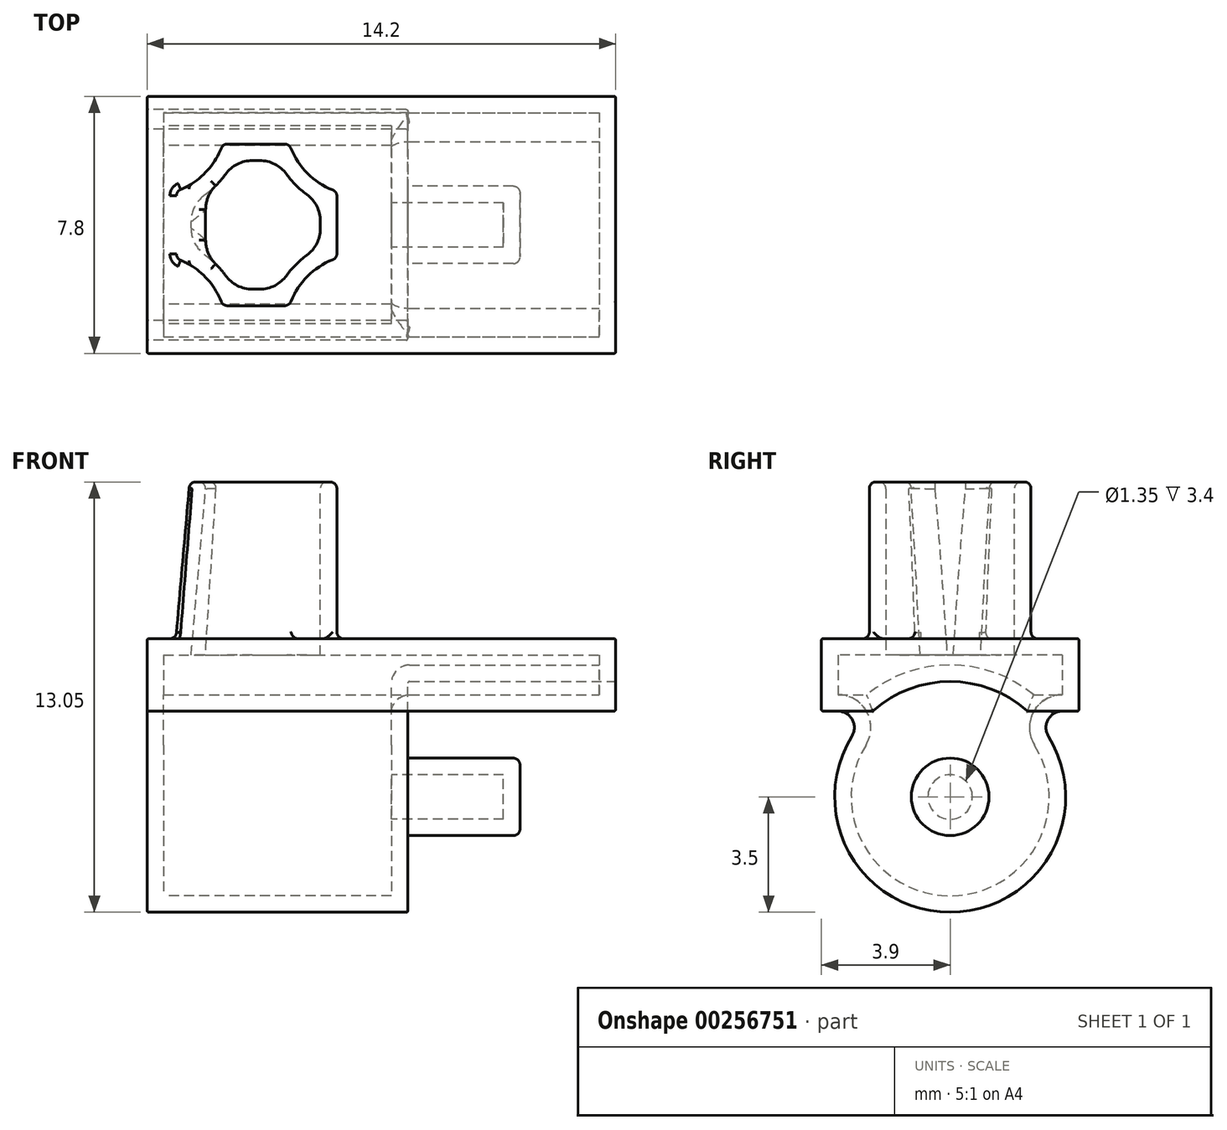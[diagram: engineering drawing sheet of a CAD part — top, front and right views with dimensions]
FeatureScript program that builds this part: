
annotation { "Feature Type Name" : "Feature", "Feature Type Description" : "" }
export const myFeature = defineFeature(function(context is Context, id is Id, definition is map)
    precondition{}
    {
        {
            var Q0;
            Q0=qCreatedBy(makeId("Right.planeOp"),FACE);
            var sketch = newSketch(context, id + "F0", { "sketchPlane" : qUnion([Q0])});
            skArc(sketch, "E0", {"start": v(-2.34, 2.6) * mm, "mid": v(0, -3.5) * mm, "end": v(2.34, 2.6) * mm});
            skLineSegment(sketch, "E1", {"start": v(-3.9, 4.8) * mm, "end": v(3.9, 4.8) * mm});
            skPoint(sketch, "E2", {"position": v(0, 4.8) * mm});
            skLineSegment(sketch, "E3", {"start": v(-3.9, 2.6) * mm, "end": v(-2.34, 2.6) * mm});
            skLineSegment(sketch, "E4", {"start": v(-3.9, 2.6) * mm, "end": v(-3.9, 4.8) * mm});
            skLineSegment(sketch, "E5", {"start": v(3.9, 2.6) * mm, "end": v(3.9, 4.8) * mm});
            skLineSegment(sketch, "E6.trimOffspring", {"start": v(2.34, 2.6) * mm, "end": v(3.9, 2.6) * mm});
            skSolve(sketch);
        }
        {
            var Q0;
            Q0=makeQuery(id+"F0.imprint","IMPRINT",FACE,{"disambiguationData":[TD([[makeQuery(id+"F0.imprint","IMPRINT",EDGE,{"derivedFrom":sQuery(id+"F0.wireOp",EDGE,"E0")}),1.0]])]});
            extrude(context, id + "F1", {"entities" : qUnion([Q0]), "depth" : 14.2 * mm, "symmetric" : true});
        }
        {
            var Q0;
            Q0=makeQuery(id+"F1.opExtrude","CAP_FACE",FACE,{"disambiguationData":[OSD([sQuery(id+"F0.wireOp",EDGE,"E0"),sQuery(id+"F0.wireOp",EDGE,"E1"),sQuery(id+"F0.wireOp",EDGE,"E3"),sQuery(id+"F0.wireOp",EDGE,"E4"),sQuery(id+"F0.wireOp",EDGE,"E5"),sQuery(id+"F0.wireOp",EDGE,"E6.trimOffspring")])],"isStart":false});
            var sketch = newSketch(context, id + "F2", { "sketchPlane" : qUnion([Q0])});
            skCircle(sketch, "E7", {"center": v(0, 0) * mm, "radius": 3.5 * mm});
            skSolve(sketch);
        }
        {
            var Q0;
            {var subQ0=sQuery(id+"F2.wireOp",EDGE,"E7");var subQ1=makeQuery(id+"F2.imprint","INTERSECT",VERTEX,{"derivedFrom":[makeQuery(id+"F1.opExtrude","CAP_EDGE",EDGE,{"disambiguationData":[OSD([sQuery(id+"F0.wireOp",EDGE,"E3")])],"isStart":false}),subQ0]});Q0=makeQuery(id+"F2.imprint","IMPRINT",FACE,{"disambiguationData":[TD([[makeQuery(id+"F2.imprint","IMPRINT",EDGE,{"disambiguationData":[TD([[subQ1,-1.0]])],"derivedFrom":subQ0}),1.0]])]});}
            extrude(context, id + "F3", {"entities" : qUnion([Q0]), "operationType" : NewBodyOperationType.REMOVE, "oppositeDirection" : true, "depth" : 6.3 * mm});
        }
        {
            var Q0;
            {var subQ0=sQuery(id+"F0.wireOp",EDGE,"E0");var subQ1=makeQuery(id+"F1.opExtrude","SWEPT_FACE",FACE,{"disambiguationData":[OSD([subQ0])]});var subQ2=sQuery(id+"F0.wireOp",EDGE,"E3");Q0=makeQuery(id+"FiiATRbnGKAqu3H_1.1.F3.boolean.opBoolean","SPLIT",EDGE,{"disambiguationData":[topologyDisambiguationEdgeConnected([subQ1])],"derivedFrom":makeQuery(id+"F3.boolean.opBoolean","SPLIT",EDGE,{"disambiguationData":[topologyDisambiguationEdgeConnected([subQ1])],"derivedFrom":makeQuery(id+"F1.opExtrude","SWEPT_EDGE",EDGE,{"disambiguationData":[OSD([subQ0,subQ2])]})})});}
            var Q1;
            {var subQ0=sQuery(id+"F0.wireOp",EDGE,"E0");var subQ1=makeQuery(id+"F1.opExtrude","SWEPT_FACE",FACE,{"disambiguationData":[OSD([subQ0])]});var subQ2=sQuery(id+"F0.wireOp",EDGE,"E6.trimOffspring");Q1=makeQuery(id+"FiiATRbnGKAqu3H_1.1.F3.boolean.opBoolean","SPLIT",EDGE,{"disambiguationData":[topologyDisambiguationEdgeConnected([subQ1])],"derivedFrom":makeQuery(id+"F3.boolean.opBoolean","SPLIT",EDGE,{"disambiguationData":[topologyDisambiguationEdgeConnected([subQ1])],"derivedFrom":makeQuery(id+"F1.opExtrude","SWEPT_EDGE",EDGE,{"disambiguationData":[OSD([subQ0,subQ2])]})})});}
            fillet(context, id + "F4", {"entities" : qUnion([Q0, Q1]), "radius" : 0.5 * mm, "tangentPropagation" : true, "allowEdgeOverflow" : false});
        }
        {
            var Q0;
            Q0=makeQuery(id+"F3.boolean.opBoolean","COPY",FACE,{"derivedFrom":makeQuery(id+"F3.opExtrude","CAP_FACE",FACE,{"disambiguationData":[OSD([sQuery(id+"F2.wireOp",EDGE,"E7")])],"isStart":false})});
            var Q1;
            Q1=makeQuery(id+"FiiATRbnGKAqu3H_1.1.F3.boolean.opBoolean","COPY",FACE,{"derivedFrom":makeQuery(id+"FiiATRbnGKAqu3H_1.1.F3.opExtrude","CAP_FACE",FACE,{"disambiguationData":[OSD([sQuery(id+"F2.wireOp",EDGE,"E7")])],"isStart":false})});
            var Q2;
            Q2=makeQuery(id+"F3.boolean.opBoolean","COPY",FACE,{"derivedFrom":makeQuery(id+"F3.opExtrude","SWEPT_FACE",FACE,{"disambiguationData":[OSD([sQuery(id+"F2.wireOp",EDGE,"E7")])]})});
            var Q3;
            Q3=makeQuery(id+"FiiATRbnGKAqu3H_1.1.F3.boolean.opBoolean","COPY",FACE,{"derivedFrom":makeQuery(id+"FiiATRbnGKAqu3H_1.1.F3.opExtrude","SWEPT_FACE",FACE,{"disambiguationData":[OSD([sQuery(id+"F2.wireOp",EDGE,"E7")])]})});
            var Q4;
            Q4=makeQuery(id+"F1.opExtrude","SWEPT_FACE",FACE,{"disambiguationData":[OSD([sQuery(id+"F0.wireOp",EDGE,"E3")])]});
            var Q5;
            Q5=makeQuery(id+"F1.opExtrude","SWEPT_FACE",FACE,{"disambiguationData":[OSD([sQuery(id+"F0.wireOp",EDGE,"E4")])]});
            var Q6;
            Q6=makeQuery(id+"F1.opExtrude","CAP_FACE",FACE,{"disambiguationData":[OSD([sQuery(id+"F0.wireOp",EDGE,"E0"),sQuery(id+"F0.wireOp",EDGE,"E1"),sQuery(id+"F0.wireOp",EDGE,"E3"),sQuery(id+"F0.wireOp",EDGE,"E4"),sQuery(id+"F0.wireOp",EDGE,"E5"),sQuery(id+"F0.wireOp",EDGE,"E6.trimOffspring")])],"isStart":false});
            var Q7;
            Q7=makeQuery(id+"F1.opExtrude","SWEPT_FACE",FACE,{"disambiguationData":[OSD([sQuery(id+"F0.wireOp",EDGE,"E6.trimOffspring")])]});
            var Q8;
            Q8=makeQuery(id+"F1.opExtrude","SWEPT_FACE",FACE,{"disambiguationData":[OSD([sQuery(id+"F0.wireOp",EDGE,"E5")])]});
            var Q9;
            Q9=makeQuery(id+"F1.opExtrude","CAP_FACE",FACE,{"disambiguationData":[OSD([sQuery(id+"F0.wireOp",EDGE,"E0"),sQuery(id+"F0.wireOp",EDGE,"E1"),sQuery(id+"F0.wireOp",EDGE,"E3"),sQuery(id+"F0.wireOp",EDGE,"E4"),sQuery(id+"F0.wireOp",EDGE,"E5"),sQuery(id+"F0.wireOp",EDGE,"E6.trimOffspring")])],"isStart":true});
            fillet(context, id + "F5", {"entities" : qUnion([Q0, Q1, Q2, Q3, Q4, Q5, Q6, Q7, Q8, Q9]), "radius" : 0.05 * mm, "tangentPropagation" : true, "allowEdgeOverflow" : false});
        }
        {
            var Q0;
            Q0=makeQuery(id+"F3.boolean.opBoolean","COPY",FACE,{"derivedFrom":makeQuery(id+"F3.opExtrude","CAP_FACE",FACE,{"disambiguationData":[OSD([sQuery(id+"F2.wireOp",EDGE,"E7")])],"isStart":false})});
            var sketch = newSketch(context, id + "F6", { "sketchPlane" : qUnion([Q0])});
            skCircle(sketch, "E8", {"center": v(0, 0) * mm, "radius": 1.18 * mm});
            skSolve(sketch);
        }
        {
            var Q0;
            Q0=makeQuery(id+"F6.imprint","IMPRINT",FACE,{"disambiguationData":[TD([[makeQuery(id+"F6.imprint","IMPRINT",EDGE,{"derivedFrom":sQuery(id+"F6.wireOp",EDGE,"E8")}),1.0]])]});
            extrude(context, id + "F7", {"entities" : qUnion([Q0]), "operationType" : NewBodyOperationType.ADD, "depth" : 3.4 * mm});
        }
        {
            var Q0;
            Q0=makeQuery(id+"F7.opExtrude","CAP_EDGE",EDGE,{"disambiguationData":[OSD([sQuery(id+"F6.wireOp",EDGE,"E8")])],"isStart":false});
            var Q1;
            Q1=makeQuery(id+"F7.opExtrude","CAP_EDGE",EDGE,{"disambiguationData":[OSD([sQuery(id+"F6.wireOp",EDGE,"E8")])],"isStart":true});
            fillet(context, id + "F8", {"entities" : qUnion([Q0, Q1]), "radius" : 0.2 * mm, "tangentPropagation" : true, "allowEdgeOverflow" : false});
        }
        {
            var Q0;
            Q0=makeQuery(id+"F1.opExtrude","SWEPT_FACE",FACE,{"disambiguationData":[OSD([sQuery(id+"F0.wireOp",EDGE,"E1")])]});
            var sketch = newSketch(context, id + "F9", { "sketchPlane" : qUnion([Q0])});
            skLineSegment(sketch, "E9.bottom", {"start": v(-4.81, 2.45) * mm, "end": v(-2.79, 2.45) * mm});
            skLineSegment(sketch, "E9.top", {"start": v(-4.81, -2.45) * mm, "end": v(-2.79, -2.45) * mm});
            skLineSegment(sketch, "E9.left", {"start": v(-6.25, 1.01) * mm, "end": v(-6.25, -1.01) * mm});
            skLineSegment(sketch, "E9.right", {"start": v(-1.35, 1.01) * mm, "end": v(-1.35, -1.01) * mm});
            skPoint(sketch, "E10", {"position": v(-1.35, 0) * mm});
            skArc(sketch, "E11", {"start": v(-2.79, 2.45) * mm, "mid": v(-2.24, 1.56) * mm, "end": v(-1.35, 1.01) * mm});
            skPoint(sketch, "E12.orphan", {"position": v(-1.35, 2.45) * mm});
            skArc(sketch, "E13", {"start": v(-1.35, -1.01) * mm, "mid": v(-2.24, -1.56) * mm, "end": v(-2.79, -2.45) * mm});
            skPoint(sketch, "E14.orphan", {"position": v(-1.35, -2.45) * mm});
            skArc(sketch, "E15", {"start": v(-6.25, 1.01) * mm, "mid": v(-5.36, 1.56) * mm, "end": v(-4.81, 2.45) * mm});
            skArc(sketch, "E16", {"start": v(-4.81, -2.45) * mm, "mid": v(-5.36, -1.56) * mm, "end": v(-6.25, -1.01) * mm});
            skSolve(sketch);
        }
        {
            var Q0;
            Q0=makeQuery(id+"F9.imprint","IMPRINT",FACE,{"disambiguationData":[TD([[makeQuery(id+"F9.imprint","IMPRINT",EDGE,{"derivedFrom":sQuery(id+"F9.wireOp",EDGE,"E9.bottom")}),-1.0]])]});
            extrude(context, id + "F10", {"entities" : qUnion([Q0]), "operationType" : NewBodyOperationType.ADD, "depth" : 4.75 * mm});
        }
        {
            var Q0;
            Q0=makeQuery(id+"F10.opExtrude","CAP_EDGE",EDGE,{"disambiguationData":[OSD([sQuery(id+"F9.wireOp",EDGE,"E9.left")])],"isStart":false});
            chamfer(context, id + "F11", {"entities" : qUnion([Q0]), "chamferType" : ChamferType.OFFSET_ANGLE, "width" : 5 * mm, "oppositeDirection" : true, "angle" : 5 * degree, "tangentPropagation" : true});
        }
        {
            var Q0;
            Q0=makeQuery(id+"F10.opExtrude","CAP_FACE",FACE,{"disambiguationData":[OSD([sQuery(id+"F9.wireOp",EDGE,"E9.bottom"),sQuery(id+"F9.wireOp",EDGE,"E9.top"),sQuery(id+"F9.wireOp",EDGE,"E9.left"),sQuery(id+"F9.wireOp",EDGE,"E9.right"),sQuery(id+"F9.wireOp",EDGE,"E11"),sQuery(id+"F9.wireOp",EDGE,"E13"),sQuery(id+"F9.wireOp",EDGE,"E15"),sQuery(id+"F9.wireOp",EDGE,"E16")])],"isStart":false});
            var Q1;
            Q1=makeQuery(id+"FyhG3hh5PRaOZG8_1.1.F10.opExtrude","CAP_FACE",FACE,{"disambiguationData":[OSD([sQuery(id+"F9.wireOp",EDGE,"E9.bottom"),sQuery(id+"F9.wireOp",EDGE,"E9.top"),sQuery(id+"F9.wireOp",EDGE,"E9.left"),sQuery(id+"F9.wireOp",EDGE,"E9.right"),sQuery(id+"F9.wireOp",EDGE,"E11"),sQuery(id+"F9.wireOp",EDGE,"E13"),sQuery(id+"F9.wireOp",EDGE,"E15"),sQuery(id+"F9.wireOp",EDGE,"E16")])],"isStart":false});
            shell(context, id + "F12", {"entities" : qUnion([Q0, Q1]), "thickness" : 0.5 * mm});
        }
        {
            var Q0;
            Q0=makeQuery(id+"F10.opExtrude","CAP_EDGE",EDGE,{"disambiguationData":[OSD([sQuery(id+"F9.wireOp",EDGE,"E16")])],"isStart":true});
            var Q1;
            Q1=makeQuery(id+"F10.opExtrude","CAP_EDGE",EDGE,{"disambiguationData":[OSD([sQuery(id+"F9.wireOp",EDGE,"E9.top")])],"isStart":true});
            var Q2;
            Q2=makeQuery(id+"F10.opExtrude","CAP_EDGE",EDGE,{"disambiguationData":[OSD([sQuery(id+"F9.wireOp",EDGE,"E13")])],"isStart":true});
            var Q3;
            Q3=makeQuery(id+"FyhG3hh5PRaOZG8_1.1.F10.opExtrude","CAP_EDGE",EDGE,{"disambiguationData":[OSD([sQuery(id+"F9.wireOp",EDGE,"E9.right")])],"isStart":true});
            var Q4;
            Q4=makeQuery(id+"FyhG3hh5PRaOZG8_1.1.F10.opExtrude","CAP_EDGE",EDGE,{"disambiguationData":[OSD([sQuery(id+"F9.wireOp",EDGE,"E13")])],"isStart":true});
            var Q5;
            Q5=makeQuery(id+"FyhG3hh5PRaOZG8_1.1.F10.opExtrude","CAP_EDGE",EDGE,{"disambiguationData":[OSD([sQuery(id+"F9.wireOp",EDGE,"E9.top")])],"isStart":true});
            var Q6;
            Q6=makeQuery(id+"FyhG3hh5PRaOZG8_1.1.F10.opExtrude","CAP_EDGE",EDGE,{"disambiguationData":[OSD([sQuery(id+"F9.wireOp",EDGE,"E16")])],"isStart":true});
            var Q7;
            Q7=makeQuery(id+"FyhG3hh5PRaOZG8_1.1.F11.opChamfer","BLEND_EDGE",EDGE,{"blendedFrom":[makeQuery(id+"FyhG3hh5PRaOZG8_1.1.F10.opExtrude","CAP_EDGE",EDGE,{"disambiguationData":[OSD([sQuery(id+"F9.wireOp",EDGE,"E9.left")])],"isStart":false}),makeQuery(id+"F1.opExtrude","SWEPT_FACE",FACE,{"disambiguationData":[OSD([sQuery(id+"F0.wireOp",EDGE,"E1")])]})],"blendedInto":[makeQuery(id+"F1.opExtrude","SWEPT_FACE",FACE,{"disambiguationData":[OSD([sQuery(id+"F0.wireOp",EDGE,"E1")])]})]});
            var Q8;
            Q8=makeQuery(id+"FyhG3hh5PRaOZG8_1.1.F10.opExtrude","CAP_EDGE",EDGE,{"disambiguationData":[OSD([sQuery(id+"F9.wireOp",EDGE,"E15")])],"isStart":true});
            var Q9;
            Q9=makeQuery(id+"FyhG3hh5PRaOZG8_1.1.F10.opExtrude","CAP_EDGE",EDGE,{"disambiguationData":[OSD([sQuery(id+"F9.wireOp",EDGE,"E9.bottom")])],"isStart":true});
            var Q10;
            Q10=makeQuery(id+"F10.opExtrude","CAP_EDGE",EDGE,{"disambiguationData":[OSD([sQuery(id+"F9.wireOp",EDGE,"E9.right")])],"isStart":true});
            var Q11;
            Q11=makeQuery(id+"F10.opExtrude","CAP_EDGE",EDGE,{"disambiguationData":[OSD([sQuery(id+"F9.wireOp",EDGE,"E11")])],"isStart":true});
            var Q12;
            Q12=makeQuery(id+"F10.opExtrude","CAP_EDGE",EDGE,{"disambiguationData":[OSD([sQuery(id+"F9.wireOp",EDGE,"E9.bottom")])],"isStart":true});
            var Q13;
            Q13=makeQuery(id+"FyhG3hh5PRaOZG8_1.1.F10.opExtrude","CAP_EDGE",EDGE,{"disambiguationData":[OSD([sQuery(id+"F9.wireOp",EDGE,"E11")])],"isStart":true});
            var Q14;
            Q14=makeQuery(id+"F10.opExtrude","CAP_EDGE",EDGE,{"disambiguationData":[OSD([sQuery(id+"F9.wireOp",EDGE,"E15")])],"isStart":true});
            var Q15;
            Q15=makeQuery(id+"F11.opChamfer","BLEND_EDGE",EDGE,{"blendedFrom":[makeQuery(id+"F10.opExtrude","CAP_EDGE",EDGE,{"disambiguationData":[OSD([sQuery(id+"F9.wireOp",EDGE,"E9.left")])],"isStart":false}),makeQuery(id+"F1.opExtrude","SWEPT_FACE",FACE,{"disambiguationData":[OSD([sQuery(id+"F0.wireOp",EDGE,"E1")])]})],"blendedInto":[makeQuery(id+"F1.opExtrude","SWEPT_FACE",FACE,{"disambiguationData":[OSD([sQuery(id+"F0.wireOp",EDGE,"E1")])]})]});
            fillet(context, id + "F13", {"entities" : qUnion([Q0, Q1, Q2, Q3, Q4, Q5, Q6, Q7, Q8, Q9, Q10, Q11, Q12, Q13, Q14, Q15]), "radius" : 0.2 * mm, "tangentPropagation" : true, "allowEdgeOverflow" : false});
        }
        {
            var Q0;
            {var subQ0=sQuery(id+"F9.wireOp",EDGE,"E16");var subQ1=sQuery(id+"F9.wireOp",EDGE,"E9.top");Q0=makeQuery(id+"F12.opShell","OFFSET_EDGE",EDGE,{"disambiguationData":[OSD([subQ1,subQ0]),TDD([makeQuery(id+"F10.opExtrude","SWEPT_EDGE",EDGE,{"disambiguationData":[OSD([subQ1,subQ0])]})])]});}
            var Q1;
            {var subQ0=sQuery(id+"F9.wireOp",EDGE,"E16");var subQ1=sQuery(id+"F9.wireOp",EDGE,"E9.left");Q1=makeQuery(id+"F12.opShell","OFFSET_EDGE",EDGE,{"disambiguationData":[OSD([subQ1,subQ0]),TDD([makeQuery(id+"F11.opChamfer","BLEND_EDGE",EDGE,{"blendedFrom":[makeQuery(id+"F10.opExtrude","CAP_EDGE",EDGE,{"disambiguationData":[OSD([subQ1])],"isStart":false}),makeQuery(id+"F10.opExtrude","SWEPT_FACE",FACE,{"disambiguationData":[OSD([subQ0])]})],"blendedInto":[makeQuery(id+"F10.opExtrude","SWEPT_FACE",FACE,{"disambiguationData":[OSD([subQ0])]})]})])]});}
            var Q2;
            {var subQ0=sQuery(id+"F9.wireOp",EDGE,"E15");var subQ1=sQuery(id+"F9.wireOp",EDGE,"E9.left");Q2=makeQuery(id+"F12.opShell","OFFSET_EDGE",EDGE,{"disambiguationData":[OSD([subQ1,subQ0]),TDD([makeQuery(id+"F11.opChamfer","BLEND_EDGE",EDGE,{"blendedFrom":[makeQuery(id+"F10.opExtrude","CAP_EDGE",EDGE,{"disambiguationData":[OSD([subQ1])],"isStart":false}),makeQuery(id+"F10.opExtrude","SWEPT_FACE",FACE,{"disambiguationData":[OSD([subQ0])]})],"blendedInto":[makeQuery(id+"F10.opExtrude","SWEPT_FACE",FACE,{"disambiguationData":[OSD([subQ0])]})]})])]});}
            var Q3;
            {var subQ0=sQuery(id+"F9.wireOp",EDGE,"E15");var subQ1=sQuery(id+"F9.wireOp",EDGE,"E9.bottom");Q3=makeQuery(id+"F12.opShell","OFFSET_EDGE",EDGE,{"disambiguationData":[OSD([subQ1,subQ0]),TDD([makeQuery(id+"F10.opExtrude","SWEPT_EDGE",EDGE,{"disambiguationData":[OSD([subQ1,subQ0])]})])]});}
            var Q4;
            {var subQ0=sQuery(id+"F9.wireOp",EDGE,"E11");var subQ1=sQuery(id+"F9.wireOp",EDGE,"E9.bottom");Q4=makeQuery(id+"F12.opShell","OFFSET_EDGE",EDGE,{"disambiguationData":[OSD([subQ1,subQ0]),TDD([makeQuery(id+"F10.opExtrude","SWEPT_EDGE",EDGE,{"disambiguationData":[OSD([subQ1,subQ0])]})])]});}
            var Q5;
            {var subQ0=sQuery(id+"F9.wireOp",EDGE,"E11");var subQ1=sQuery(id+"F9.wireOp",EDGE,"E9.right");Q5=makeQuery(id+"F12.opShell","OFFSET_EDGE",EDGE,{"disambiguationData":[OSD([subQ1,subQ0]),TDD([makeQuery(id+"F10.opExtrude","SWEPT_EDGE",EDGE,{"disambiguationData":[OSD([subQ1,subQ0])]})])]});}
            var Q6;
            {var subQ0=sQuery(id+"F9.wireOp",EDGE,"E13");var subQ1=sQuery(id+"F9.wireOp",EDGE,"E9.right");Q6=makeQuery(id+"F12.opShell","OFFSET_EDGE",EDGE,{"disambiguationData":[OSD([subQ1,subQ0]),TDD([makeQuery(id+"F10.opExtrude","SWEPT_EDGE",EDGE,{"disambiguationData":[OSD([subQ1,subQ0])]})])]});}
            var Q7;
            {var subQ0=sQuery(id+"F9.wireOp",EDGE,"E13");var subQ1=sQuery(id+"F9.wireOp",EDGE,"E9.top");Q7=makeQuery(id+"F12.opShell","OFFSET_EDGE",EDGE,{"disambiguationData":[OSD([subQ1,subQ0]),TDD([makeQuery(id+"F10.opExtrude","SWEPT_EDGE",EDGE,{"disambiguationData":[OSD([subQ1,subQ0])]})])]});}
            var Q8;
            {var subQ0=sQuery(id+"F9.wireOp",EDGE,"E15");var subQ1=sQuery(id+"F9.wireOp",EDGE,"E9.left");Q8=makeQuery(id+"F12.opShell","OFFSET_EDGE",EDGE,{"disambiguationData":[OSD([subQ1,subQ0]),TDD([makeQuery(id+"FyhG3hh5PRaOZG8_1.1.F11.opChamfer","BLEND_EDGE",EDGE,{"blendedFrom":[makeQuery(id+"FyhG3hh5PRaOZG8_1.1.F10.opExtrude","CAP_EDGE",EDGE,{"disambiguationData":[OSD([subQ1])],"isStart":false}),makeQuery(id+"FyhG3hh5PRaOZG8_1.1.F10.opExtrude","SWEPT_FACE",FACE,{"disambiguationData":[OSD([subQ0])]})],"blendedInto":[makeQuery(id+"FyhG3hh5PRaOZG8_1.1.F10.opExtrude","SWEPT_FACE",FACE,{"disambiguationData":[OSD([subQ0])]})]})])]});}
            var Q9;
            {var subQ0=sQuery(id+"F9.wireOp",EDGE,"E16");var subQ1=sQuery(id+"F9.wireOp",EDGE,"E9.left");Q9=makeQuery(id+"F12.opShell","OFFSET_EDGE",EDGE,{"disambiguationData":[OSD([subQ1,subQ0]),TDD([makeQuery(id+"FyhG3hh5PRaOZG8_1.1.F11.opChamfer","BLEND_EDGE",EDGE,{"blendedFrom":[makeQuery(id+"FyhG3hh5PRaOZG8_1.1.F10.opExtrude","CAP_EDGE",EDGE,{"disambiguationData":[OSD([subQ1])],"isStart":false}),makeQuery(id+"FyhG3hh5PRaOZG8_1.1.F10.opExtrude","SWEPT_FACE",FACE,{"disambiguationData":[OSD([subQ0])]})],"blendedInto":[makeQuery(id+"FyhG3hh5PRaOZG8_1.1.F10.opExtrude","SWEPT_FACE",FACE,{"disambiguationData":[OSD([subQ0])]})]})])]});}
            var Q10;
            {var subQ0=sQuery(id+"F9.wireOp",EDGE,"E16");var subQ1=sQuery(id+"F9.wireOp",EDGE,"E9.top");Q10=makeQuery(id+"F12.opShell","OFFSET_EDGE",EDGE,{"disambiguationData":[OSD([subQ1,subQ0]),TDD([makeQuery(id+"FyhG3hh5PRaOZG8_1.1.F10.opExtrude","SWEPT_EDGE",EDGE,{"disambiguationData":[OSD([subQ1,subQ0])]})])]});}
            var Q11;
            {var subQ0=sQuery(id+"F9.wireOp",EDGE,"E13");var subQ1=sQuery(id+"F9.wireOp",EDGE,"E9.top");Q11=makeQuery(id+"F12.opShell","OFFSET_EDGE",EDGE,{"disambiguationData":[OSD([subQ1,subQ0]),TDD([makeQuery(id+"FyhG3hh5PRaOZG8_1.1.F10.opExtrude","SWEPT_EDGE",EDGE,{"disambiguationData":[OSD([subQ1,subQ0])]})])]});}
            var Q12;
            {var subQ0=sQuery(id+"F9.wireOp",EDGE,"E13");var subQ1=sQuery(id+"F9.wireOp",EDGE,"E9.right");Q12=makeQuery(id+"F12.opShell","OFFSET_EDGE",EDGE,{"disambiguationData":[OSD([subQ1,subQ0]),TDD([makeQuery(id+"FyhG3hh5PRaOZG8_1.1.F10.opExtrude","SWEPT_EDGE",EDGE,{"disambiguationData":[OSD([subQ1,subQ0])]})])]});}
            var Q13;
            {var subQ0=sQuery(id+"F9.wireOp",EDGE,"E11");var subQ1=sQuery(id+"F9.wireOp",EDGE,"E9.right");Q13=makeQuery(id+"F12.opShell","OFFSET_EDGE",EDGE,{"disambiguationData":[OSD([subQ1,subQ0]),TDD([makeQuery(id+"FyhG3hh5PRaOZG8_1.1.F10.opExtrude","SWEPT_EDGE",EDGE,{"disambiguationData":[OSD([subQ1,subQ0])]})])]});}
            var Q14;
            {var subQ0=sQuery(id+"F9.wireOp",EDGE,"E11");var subQ1=sQuery(id+"F9.wireOp",EDGE,"E9.bottom");Q14=makeQuery(id+"F12.opShell","OFFSET_EDGE",EDGE,{"disambiguationData":[OSD([subQ1,subQ0]),TDD([makeQuery(id+"FyhG3hh5PRaOZG8_1.1.F10.opExtrude","SWEPT_EDGE",EDGE,{"disambiguationData":[OSD([subQ1,subQ0])]})])]});}
            var Q15;
            {var subQ0=sQuery(id+"F9.wireOp",EDGE,"E15");var subQ1=sQuery(id+"F9.wireOp",EDGE,"E9.bottom");Q15=makeQuery(id+"F12.opShell","OFFSET_EDGE",EDGE,{"disambiguationData":[OSD([subQ1,subQ0]),TDD([makeQuery(id+"FyhG3hh5PRaOZG8_1.1.F10.opExtrude","SWEPT_EDGE",EDGE,{"disambiguationData":[OSD([subQ1,subQ0])]})])]});}
            fillet(context, id + "F14", {"entities" : qUnion([Q0, Q1, Q2, Q3, Q4, Q5, Q6, Q7, Q8, Q9, Q10, Q11, Q12, Q13, Q14, Q15]), "radius" : 1 * mm, "tangentPropagation" : true, "allowEdgeOverflow" : false});
        }
        {
            var Q0;
            Q0=makeQuery(id+"FyhG3hh5PRaOZG8_1.1.F11.opChamfer","BLEND_FACE",FACE,{"disambiguationData":[OSD([sQuery(id+"F9.wireOp",EDGE,"E9.left")])]});
            var Q1;
            Q1=makeQuery(id+"FyhG3hh5PRaOZG8_1.1.F10.opExtrude","SWEPT_FACE",FACE,{"disambiguationData":[OSD([sQuery(id+"F9.wireOp",EDGE,"E15")])]});
            var Q2;
            Q2=makeQuery(id+"FyhG3hh5PRaOZG8_1.1.F10.opExtrude","SWEPT_FACE",FACE,{"disambiguationData":[OSD([sQuery(id+"F9.wireOp",EDGE,"E9.bottom")])]});
            var Q3;
            Q3=makeQuery(id+"FyhG3hh5PRaOZG8_1.1.F10.opExtrude","SWEPT_FACE",FACE,{"disambiguationData":[OSD([sQuery(id+"F9.wireOp",EDGE,"E11")])]});
            var Q4;
            Q4=makeQuery(id+"F10.opExtrude","SWEPT_FACE",FACE,{"disambiguationData":[OSD([sQuery(id+"F9.wireOp",EDGE,"E9.right")])]});
            var Q5;
            Q5=makeQuery(id+"F10.opExtrude","SWEPT_FACE",FACE,{"disambiguationData":[OSD([sQuery(id+"F9.wireOp",EDGE,"E11")])]});
            var Q6;
            Q6=makeQuery(id+"F10.opExtrude","SWEPT_FACE",FACE,{"disambiguationData":[OSD([sQuery(id+"F9.wireOp",EDGE,"E9.bottom")])]});
            var Q7;
            Q7=makeQuery(id+"F10.opExtrude","SWEPT_FACE",FACE,{"disambiguationData":[OSD([sQuery(id+"F9.wireOp",EDGE,"E15")])]});
            var Q8;
            Q8=makeQuery(id+"F11.opChamfer","BLEND_FACE",FACE,{"disambiguationData":[OSD([sQuery(id+"F9.wireOp",EDGE,"E9.left")])]});
            var Q9;
            Q9=makeQuery(id+"F10.opExtrude","SWEPT_FACE",FACE,{"disambiguationData":[OSD([sQuery(id+"F9.wireOp",EDGE,"E16")])]});
            var Q10;
            Q10=makeQuery(id+"F10.opExtrude","SWEPT_FACE",FACE,{"disambiguationData":[OSD([sQuery(id+"F9.wireOp",EDGE,"E9.top")])]});
            var Q11;
            Q11=makeQuery(id+"FyhG3hh5PRaOZG8_1.1.F10.opExtrude","SWEPT_FACE",FACE,{"disambiguationData":[OSD([sQuery(id+"F9.wireOp",EDGE,"E9.right")])]});
            var Q12;
            Q12=makeQuery(id+"FyhG3hh5PRaOZG8_1.1.F10.opExtrude","SWEPT_FACE",FACE,{"disambiguationData":[OSD([sQuery(id+"F9.wireOp",EDGE,"E13")])]});
            var Q13;
            Q13=makeQuery(id+"FyhG3hh5PRaOZG8_1.1.F10.opExtrude","SWEPT_FACE",FACE,{"disambiguationData":[OSD([sQuery(id+"F9.wireOp",EDGE,"E9.top")])]});
            var Q14;
            Q14=makeQuery(id+"FyhG3hh5PRaOZG8_1.1.F10.opExtrude","CAP_FACE",FACE,{"disambiguationData":[OSD([sQuery(id+"F9.wireOp",EDGE,"E9.bottom"),sQuery(id+"F9.wireOp",EDGE,"E9.top"),sQuery(id+"F9.wireOp",EDGE,"E9.left"),sQuery(id+"F9.wireOp",EDGE,"E9.right"),sQuery(id+"F9.wireOp",EDGE,"E11"),sQuery(id+"F9.wireOp",EDGE,"E13"),sQuery(id+"F9.wireOp",EDGE,"E15"),sQuery(id+"F9.wireOp",EDGE,"E16")])],"isStart":false});
            var Q15;
            Q15=makeQuery(id+"F10.opExtrude","CAP_FACE",FACE,{"disambiguationData":[OSD([sQuery(id+"F9.wireOp",EDGE,"E9.bottom"),sQuery(id+"F9.wireOp",EDGE,"E9.top"),sQuery(id+"F9.wireOp",EDGE,"E9.left"),sQuery(id+"F9.wireOp",EDGE,"E9.right"),sQuery(id+"F9.wireOp",EDGE,"E11"),sQuery(id+"F9.wireOp",EDGE,"E13"),sQuery(id+"F9.wireOp",EDGE,"E15"),sQuery(id+"F9.wireOp",EDGE,"E16")])],"isStart":false});
            fillet(context, id + "F15", {"entities" : qUnion([Q0, Q1, Q2, Q3, Q4, Q5, Q6, Q7, Q8, Q9, Q10, Q11, Q12, Q13, Q14, Q15]), "radius" : 0.2 * mm, "tangentPropagation" : true, "allowEdgeOverflow" : false});
        }
    });
